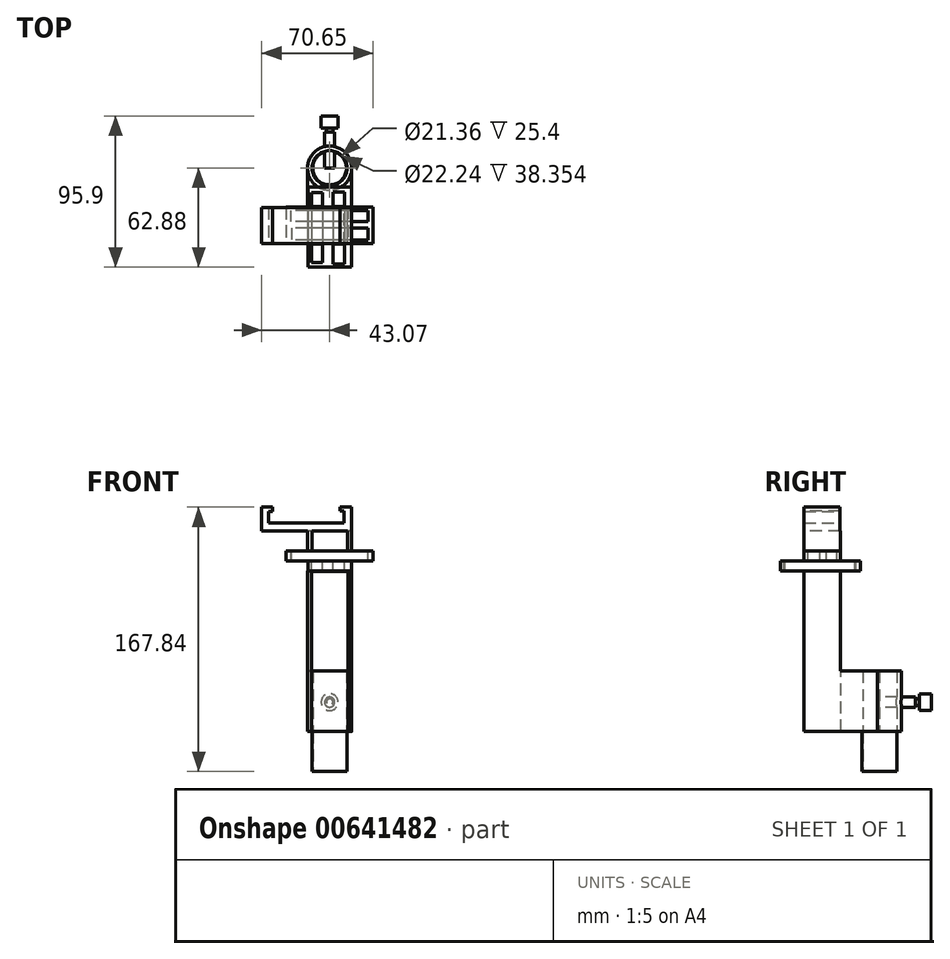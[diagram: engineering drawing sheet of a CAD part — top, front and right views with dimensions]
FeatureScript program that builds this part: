
annotation { "Feature Type Name" : "Feature", "Feature Type Description" : "" }
export const myFeature = defineFeature(function(context is Context, id is Id, definition is map)
    precondition{}
    {
        {
            var Q0;
            Q0=qCreatedBy(makeId("Top.planeOp"),FACE);
            var sketch = newSketch(context, id + "F0", { "sketchPlane" : qUnion([Q0])});
            skCircle(sketch, "E0", {"center": v(0, 0) * mm, "radius": 11.49 * mm});
            skSolve(sketch);
        }
        {
            var Q0;
            Q0=makeQuery(id+"F0.imprint","IMPRINT",FACE,{"disambiguationData":[TD([[makeQuery(id+"F0.imprint","IMPRINT",EDGE,{"derivedFrom":sQuery(id+"F0.wireOp",EDGE,"E0")}),1.0]])]});
            extrude(context, id + "F1", {"entities" : qUnion([Q0]), "depth" : 25.4 * mm, "offsetDistance" : 25.4 * mm});
        }
        {
            var Q0;
            Q0=qCreatedBy(makeId("Top.planeOp"),FACE);
            var sketch = newSketch(context, id + "F2", { "sketchPlane" : qUnion([Q0])});
            skCircle(sketch, "E1", {"center": v(0, 0) * mm, "radius": 14.04 * mm});
            skSolve(sketch);
        }
        {
            var Q0;
            Q0=makeQuery(id+"F2.imprint","IMPRINT",FACE,{"disambiguationData":[TD([[makeQuery(id+"F2.imprint","IMPRINT",EDGE,{"derivedFrom":sQuery(id+"F2.wireOp",EDGE,"E1")}),1.0]])]});
            extrude(context, id + "F3", {"entities" : qUnion([Q0]), "depth" : 38.35 * mm, "offsetDistance" : 25.4 * mm});
        }
        {
            var Q0;
            Q0=qCreatedBy(makeId("Top.planeOp"),FACE);
            var sketch = newSketch(context, id + "F4", { "sketchPlane" : qUnion([Q0])});
            skCircle(sketch, "E2", {"center": v(0, 0) * mm, "radius": 11.12 * mm});
            skSolve(sketch);
        }
        {
            var Q0;
            Q0=makeQuery(id+"F4.imprint","IMPRINT",FACE,{"disambiguationData":[TD([[makeQuery(id+"F4.imprint","IMPRINT",EDGE,{"derivedFrom":sQuery(id+"F4.wireOp",EDGE,"E2")}),1.0]])]});
            extrude(context, id + "F5", {"entities" : qUnion([Q0]), "operationType" : NewBodyOperationType.REMOVE, "depth" : 40.64 * mm, "offsetDistance" : 25.4 * mm});
        }
        {
            var Q0;
            Q0=qCreatedBy(makeId("Top.planeOp"),FACE);
            var sketch = newSketch(context, id + "F6", { "sketchPlane" : qUnion([Q0])});
            skCircle(sketch, "E3", {"center": v(0, 0) * mm, "radius": 11.14 * mm});
            skSolve(sketch);
        }
        {
            var Q0;
            Q0=makeQuery(id+"F6.imprint","IMPRINT",FACE,{"disambiguationData":[TD([[makeQuery(id+"F6.imprint","IMPRINT",EDGE,{"derivedFrom":sQuery(id+"F6.wireOp",EDGE,"E3")}),1.0]])]});
            extrude(context, id + "F7", {"entities" : qUnion([Q0]), "oppositeDirection" : true, "depth" : 25.4 * mm, "offsetDistance" : 25.4 * mm});
        }
        {
            var Q0;
            Q0=makeQuery(id+"F7.opExtrude","CAP_FACE",FACE,{"disambiguationData":[OSD([sQuery(id+"F6.wireOp",EDGE,"E3")])],"isStart":false});
            var sketch = newSketch(context, id + "F8", { "sketchPlane" : qUnion([Q0])});
            skCircle(sketch, "E4", {"center": v(0, 0) * mm, "radius": 10.68 * mm});
            skSolve(sketch);
        }
        {
            var Q0;
            Q0=makeQuery(id+"F8.imprint","IMPRINT",FACE,{"disambiguationData":[TD([[makeQuery(id+"F8.imprint","IMPRINT",EDGE,{"derivedFrom":sQuery(id+"F8.wireOp",EDGE,"E4")}),1.0]])]});
            extrude(context, id + "F9", {"entities" : qUnion([Q0]), "operationType" : NewBodyOperationType.REMOVE, "oppositeDirection" : true, "depth" : 25.4 * mm, "offsetDistance" : 25.4 * mm});
        }
        {
            var Q0;
            Q0=qCreatedBy(makeId("Right.planeOp"),FACE);
            var sketch = newSketch(context, id + "F10", { "sketchPlane" : qUnion([Q0])});
            skLineSegment(sketch, "E5.bottom", {"start": v(0, 38.3) * mm, "end": v(-48.18, 38.3) * mm});
            skLineSegment(sketch, "E5.top", {"start": v(0, 0) * mm, "end": v(-48.18, 0) * mm});
            skLineSegment(sketch, "E5.left", {"start": v(0, 38.3) * mm, "end": v(0, 0) * mm});
            skLineSegment(sketch, "E5.right", {"start": v(-48.18, 38.3) * mm, "end": v(-48.18, 0) * mm});
            skSolve(sketch);
        }
        {
            var Q0;
            Q0=makeQuery(id+"F10.imprint","IMPRINT",FACE,{"disambiguationData":[TD([[makeQuery(id+"F10.imprint","IMPRINT",EDGE,{"derivedFrom":sQuery(id+"F10.wireOp",EDGE,"E5.bottom")}),1.0]])]});
            extrude(context, id + "F11", {"entities" : qUnion([Q0]), "operationType" : NewBodyOperationType.ADD, "depth" : 13.97 * mm, "offsetDistance" : 25.4 * mm, "hasSecondDirection" : true, "secondDirectionOppositeDirection" : true, "secondDirectionDepth" : 13.97 * mm});
        }
        {
            var Q0;
            Q0=makeQuery(id+"F11.opExtrude","SWEPT_FACE",FACE,{"disambiguationData":[OSD([sQuery(id+"F10.wireOp",EDGE,"E5.bottom")])]});
            var sketch = newSketch(context, id + "F12", { "sketchPlane" : qUnion([Q0])});
            skLineSegment(sketch, "E6.bottom", {"start": v(13.97, -48.18) * mm, "end": v(-13.97, -48.18) * mm});
            skLineSegment(sketch, "E6.top", {"start": v(13.97, -24.78) * mm, "end": v(-13.97, -24.78) * mm});
            skLineSegment(sketch, "E6.left", {"start": v(13.97, -48.18) * mm, "end": v(13.97, -24.78) * mm});
            skLineSegment(sketch, "E6.right", {"start": v(-13.97, -48.18) * mm, "end": v(-13.97, -24.78) * mm});
            skSolve(sketch);
        }
        {
            var Q0;
            Q0=makeQuery(id+"F12.imprint","IMPRINT",FACE,{"disambiguationData":[TD([[makeQuery(id+"F12.imprint","IMPRINT",EDGE,{"derivedFrom":sQuery(id+"F12.wireOp",EDGE,"E6.bottom")}),-1.0]])]});
            extrude(context, id + "F13", {"entities" : qUnion([Q0]), "operationType" : NewBodyOperationType.ADD, "depth" : 63.5 * mm, "offsetDistance" : 25.4 * mm});
        }
        {
            var Q0;
            Q0=makeQuery(id+"F13.opExtrude","CAP_FACE",FACE,{"disambiguationData":[OSD([sQuery(id+"F12.wireOp",EDGE,"E6.bottom"),sQuery(id+"F12.wireOp",EDGE,"E6.top"),sQuery(id+"F12.wireOp",EDGE,"E6.left"),sQuery(id+"F12.wireOp",EDGE,"E6.right")])],"isStart":false});
            var sketch = newSketch(context, id + "F14", { "sketchPlane" : qUnion([Q0])});
            skLineSegment(sketch, "E7.bottom", {"start": v(13.78, -12.05) * mm, "end": v(-13.78, -12.05) * mm});
            skLineSegment(sketch, "E7.top", {"start": v(13.78, -62.88) * mm, "end": v(-13.78, -62.88) * mm});
            skLineSegment(sketch, "E7.left", {"start": v(13.78, -12.05) * mm, "end": v(13.78, -62.88) * mm});
            skLineSegment(sketch, "E7.right", {"start": v(-13.78, -12.05) * mm, "end": v(-13.78, -62.88) * mm});
            skPoint(sketch, "E7.middle", {"position": v(0, -37.47) * mm});
            skSolve(sketch);
        }
        {
            var Q0;
            {var subQ0=sQuery(id+"F14.wireOp",EDGE,"E7.bottom");Q0=makeQuery(id+"F14.imprint","IMPRINT",FACE,{"disambiguationData":[TD([[makeQuery(id+"F14.imprint","IMPRINT",EDGE,{"derivedFrom":subQ0}),1.0]])]});}
            var Q1;
            {var subQ0=sQuery(id+"F14.wireOp",EDGE,"E7.left");var subQ1=makeQuery(id+"F13.opExtrude","CAP_EDGE",EDGE,{"disambiguationData":[OSD([sQuery(id+"F12.wireOp",EDGE,"E6.top")])],"isStart":false});var subQ2=makeQuery(id+"F14.imprint","INTERSECT",VERTEX,{"derivedFrom":[subQ1,subQ0]});Q1=makeQuery(id+"F14.imprint","IMPRINT",FACE,{"disambiguationData":[TD([[makeQuery(id+"F14.imprint","IMPRINT",EDGE,{"disambiguationData":[TD([[subQ2,-1.0]])],"derivedFrom":subQ0}),-1.0]])]});}
            var Q2;
            {var subQ0=sQuery(id+"F14.wireOp",EDGE,"E7.top");Q2=makeQuery(id+"F14.imprint","IMPRINT",FACE,{"disambiguationData":[TD([[makeQuery(id+"F14.imprint","IMPRINT",EDGE,{"derivedFrom":subQ0}),-1.0]])]});}
            extrude(context, id + "F15", {"entities" : qUnion([Q0, Q1, Q2]), "operationType" : NewBodyOperationType.ADD, "depth" : 6.35 * mm, "offsetDistance" : 25.4 * mm});
        }
        {
            var Q0;
            Q0=makeQuery(id+"F15.opExtrude","CAP_FACE",FACE,{"disambiguationData":[OSD([sQuery(id+"F14.wireOp",EDGE,"E7.bottom"),sQuery(id+"F14.wireOp",EDGE,"E7.top"),sQuery(id+"F14.wireOp",EDGE,"E7.left"),sQuery(id+"F14.wireOp",EDGE,"E7.right")])],"isStart":false});
            var sketch = newSketch(context, id + "F16", { "sketchPlane" : qUnion([Q0])});
            skLineSegment(sketch, "E8.bottom", {"start": v(9.53, -15.14) * mm, "end": v(2.3, -15.14) * mm});
            skLineSegment(sketch, "E8.top", {"start": v(9.53, -60.82) * mm, "end": v(2.3, -60.82) * mm});
            skLineSegment(sketch, "E8.left", {"start": v(9.53, -15.14) * mm, "end": v(9.53, -60.82) * mm});
            skLineSegment(sketch, "E8.right", {"start": v(2.3, -15.14) * mm, "end": v(2.3, -60.82) * mm});
            skLineSegment(sketch, "E9.bottom", {"start": v(-4.6, -15.64) * mm, "end": v(-11.57, -15.64) * mm});
            skLineSegment(sketch, "E9.top", {"start": v(-4.6, -60.01) * mm, "end": v(-11.57, -60.01) * mm});
            skLineSegment(sketch, "E9.left", {"start": v(-4.6, -15.64) * mm, "end": v(-4.6, -60.01) * mm});
            skLineSegment(sketch, "E9.right", {"start": v(-11.57, -15.64) * mm, "end": v(-11.57, -60.01) * mm});
            skSolve(sketch);
        }
        {
            var Q0;
            Q0 = qSketchRegion(id + "F16", true);
            extrude(context, id + "F17", {"entities" : qUnion([Q0]), "operationType" : NewBodyOperationType.REMOVE, "oppositeDirection" : true, "depth" : 6.35 * mm, "offsetDistance" : 25.4 * mm});
        }
        {
            var Q0;
            Q0=makeQuery(id+"F15.opExtrude","CAP_FACE",FACE,{"disambiguationData":[OSD([sQuery(id+"F14.wireOp",EDGE,"E7.bottom"),sQuery(id+"F14.wireOp",EDGE,"E7.top"),sQuery(id+"F14.wireOp",EDGE,"E7.left"),sQuery(id+"F14.wireOp",EDGE,"E7.right")])],"isStart":false});
            var sketch = newSketch(context, id + "F18", { "sketchPlane" : qUnion([Q0])});
            skLineSegment(sketch, "E10.bottom", {"start": v(27.58, -24.72) * mm, "end": v(-27.58, -24.72) * mm});
            skLineSegment(sketch, "E10.top", {"start": v(27.58, -47.95) * mm, "end": v(-27.58, -47.95) * mm});
            skLineSegment(sketch, "E10.left", {"start": v(27.58, -24.72) * mm, "end": v(27.58, -47.95) * mm});
            skLineSegment(sketch, "E10.right", {"start": v(-27.58, -24.72) * mm, "end": v(-27.58, -47.95) * mm});
            skPoint(sketch, "E10.middle", {"position": v(0, -36.33) * mm});
            skSolve(sketch);
        }
        {
            var Q0;
            Q0 = qSketchRegion(id + "F18", true);
            extrude(context, id + "F19", {"entities" : qUnion([Q0]), "operationType" : NewBodyOperationType.ADD, "depth" : 6.35 * mm, "offsetDistance" : 25.4 * mm});
        }
        {
            var Q0;
            Q0=makeQuery(id+"F19.opExtrude","CAP_FACE",FACE,{"disambiguationData":[OSD([sQuery(id+"F18.wireOp",EDGE,"E10.bottom"),sQuery(id+"F18.wireOp",EDGE,"E10.top"),sQuery(id+"F18.wireOp",EDGE,"E10.left"),sQuery(id+"F18.wireOp",EDGE,"E10.right")])],"isStart":false});
            var sketch = newSketch(context, id + "F20", { "sketchPlane" : qUnion([Q0])});
            skLineSegment(sketch, "E11.bottom", {"start": v(24.36, -33.9) * mm, "end": v(-24.36, -33.9) * mm});
            skLineSegment(sketch, "E11.top", {"start": v(24.36, -27.03) * mm, "end": v(-24.36, -27.03) * mm});
            skLineSegment(sketch, "E11.left", {"start": v(24.36, -33.9) * mm, "end": v(24.36, -27.03) * mm});
            skLineSegment(sketch, "E11.right", {"start": v(-24.36, -33.9) * mm, "end": v(-24.36, -27.03) * mm});
            skPoint(sketch, "E11.middle", {"position": v(0, -30.46) * mm});
            skPoint(sketch, "E11.middle.positionSnap0", {"position": v(0, -24.72) * mm});
            skPoint(sketch, "E11.centerSnap0", {"position": v(0, -24.72) * mm});
            skLineSegment(sketch, "E12.bottom", {"start": v(24.3, -38.01) * mm, "end": v(-24.3, -38.01) * mm});
            skLineSegment(sketch, "E12.top", {"start": v(24.3, -45.63) * mm, "end": v(-24.3, -45.63) * mm});
            skLineSegment(sketch, "E12.left", {"start": v(24.3, -38.01) * mm, "end": v(24.3, -45.63) * mm});
            skLineSegment(sketch, "E12.right", {"start": v(-24.3, -38.01) * mm, "end": v(-24.3, -45.63) * mm});
            skPoint(sketch, "E12.middle", {"position": v(0, -41.82) * mm});
            skPoint(sketch, "E12.middle.positionSnap0", {"position": v(0, -33.9) * mm});
            skPoint(sketch, "E12.centerSnap0", {"position": v(0, -33.9) * mm});
            skSolve(sketch);
        }
        {
            var Q0;
            Q0=makeQuery(id+"F20.imprint","IMPRINT",FACE,{"disambiguationData":[TD([[makeQuery(id+"F20.imprint","IMPRINT",EDGE,{"derivedFrom":sQuery(id+"F20.wireOp",EDGE,"E11.bottom")}),-1.0]])]});
            var Q1;
            Q1=makeQuery(id+"F20.imprint","IMPRINT",FACE,{"disambiguationData":[TD([[makeQuery(id+"F20.imprint","IMPRINT",EDGE,{"derivedFrom":sQuery(id+"F20.wireOp",EDGE,"E12.bottom")}),1.0]])]});
            extrude(context, id + "F21", {"entities" : qUnion([Q0, Q1]), "operationType" : NewBodyOperationType.REMOVE, "oppositeDirection" : true, "depth" : 6.35 * mm, "offsetDistance" : 25.4 * mm});
        }
        {
            var Q0;
            Q0=makeQuery(id+"F13.boolean.opBoolean","MERGE",FACE,{"derivedFrom":[makeQuery(id+"F11.opExtrude","SWEPT_FACE",FACE,{"disambiguationData":[OSD([sQuery(id+"F10.wireOp",EDGE,"E5.right")])]}),makeQuery(id+"F13.opExtrude","SWEPT_FACE",FACE,{"disambiguationData":[OSD([sQuery(id+"F12.wireOp",EDGE,"E6.bottom")])]})]});
            var sketch = newSketch(context, id + "F22", { "sketchPlane" : qUnion([Q0])});
            skLineSegment(sketch, "E13.bottom", {"start": v(-11.56, -7.42) * mm, "end": v(11.56, -7.42) * mm});
            skLineSegment(sketch, "E13.top", {"start": v(-11.56, 101.74) * mm, "end": v(11.56, 101.74) * mm});
            skLineSegment(sketch, "E13.left", {"start": v(-11.56, -7.42) * mm, "end": v(-11.56, 101.74) * mm});
            skLineSegment(sketch, "E13.right", {"start": v(11.56, -7.42) * mm, "end": v(11.56, 101.74) * mm});
            skPoint(sketch, "E13.middle", {"position": v(0, 47.16) * mm});
            skSolve(sketch);
        }
        {
            var Q0;
            {var subQ0=sQuery(id+"F22.wireOp",EDGE,"E13.top");Q0=makeQuery(id+"F22.imprint","IMPRINT",FACE,{"disambiguationData":[TD([[makeQuery(id+"F22.imprint","IMPRINT",EDGE,{"derivedFrom":subQ0}),-1.0]])]});}
            extrude(context, id + "F23", {"entities" : qUnion([Q0]), "operationType" : NewBodyOperationType.REMOVE, "oppositeDirection" : true, "depth" : 23.62 * mm, "offsetDistance" : 25.4 * mm});
        }
        {
            var Q0;
            Q0=makeQuery(id+"F19.opExtrude","CAP_FACE",FACE,{"disambiguationData":[OSD([sQuery(id+"F18.wireOp",EDGE,"E10.bottom"),sQuery(id+"F18.wireOp",EDGE,"E10.top"),sQuery(id+"F18.wireOp",EDGE,"E10.left"),sQuery(id+"F18.wireOp",EDGE,"E10.right")])],"isStart":false});
            var sketch = newSketch(context, id + "F24", { "sketchPlane" : qUnion([Q0])});
            skLineSegment(sketch, "E14.bottom", {"start": v(-14, -24.72) * mm, "end": v(14, -24.72) * mm});
            skLineSegment(sketch, "E14.top", {"start": v(-14, -48) * mm, "end": v(14, -48) * mm});
            skLineSegment(sketch, "E14.left", {"start": v(-14, -24.72) * mm, "end": v(-14, -48) * mm});
            skLineSegment(sketch, "E14.right", {"start": v(14, -24.72) * mm, "end": v(14, -48) * mm});
            skPoint(sketch, "E14.middle", {"position": v(0, -36.36) * mm});
            skSolve(sketch);
        }
        {
            var Q0;
            Q0 = qSketchRegion(id + "F24", true);
            extrude(context, id + "F25", {"entities" : qUnion([Q0]), "operationType" : NewBodyOperationType.ADD, "depth" : 12.7 * mm, "offsetDistance" : 25.4 * mm});
        }
        {
            var Q0;
            Q0=makeQuery(id+"F25.opExtrude","CAP_FACE",FACE,{"disambiguationData":[OSD([sQuery(id+"F24.wireOp",EDGE,"E14.bottom"),sQuery(id+"F24.wireOp",EDGE,"E14.top"),sQuery(id+"F24.wireOp",EDGE,"E14.left"),sQuery(id+"F24.wireOp",EDGE,"E14.right")])],"isStart":false});
            var sketch = newSketch(context, id + "F26", { "sketchPlane" : qUnion([Q0])});
            skLineSegment(sketch, "E15.bottom", {"start": v(11.28, -50.66) * mm, "end": v(-11.28, -50.66) * mm});
            skLineSegment(sketch, "E15.top", {"start": v(11.28, -23.7) * mm, "end": v(-11.28, -23.7) * mm});
            skLineSegment(sketch, "E15.left", {"start": v(11.28, -50.66) * mm, "end": v(11.28, -23.7) * mm});
            skLineSegment(sketch, "E15.right", {"start": v(-11.28, -50.66) * mm, "end": v(-11.28, -23.7) * mm});
            skPoint(sketch, "E15.middle", {"position": v(0, -37.18) * mm});
            skSolve(sketch);
        }
        {
            var Q0;
            {var subQ0=sQuery(id+"F26.wireOp",EDGE,"E15.bottom");Q0=makeQuery(id+"F26.imprint","IMPRINT",FACE,{"disambiguationData":[TD([[makeQuery(id+"F26.imprint","IMPRINT",EDGE,{"derivedFrom":subQ0}),-1.0]])]});}
            var Q1;
            {var subQ0=sQuery(id+"F26.wireOp",EDGE,"E15.left");var subQ1=makeQuery(id+"F25.opExtrude","CAP_EDGE",EDGE,{"disambiguationData":[OSD([sQuery(id+"F24.wireOp",EDGE,"E14.top")])],"isStart":false});var subQ2=makeQuery(id+"F26.imprint","INTERSECT",VERTEX,{"derivedFrom":[subQ1,subQ0]});Q1=makeQuery(id+"F26.imprint","IMPRINT",FACE,{"disambiguationData":[TD([[makeQuery(id+"F26.imprint","IMPRINT",EDGE,{"disambiguationData":[TD([[subQ2,-1.0]])],"derivedFrom":subQ0}),1.0]])]});}
            extrude(context, id + "F27", {"entities" : qUnion([Q0, Q1]), "operationType" : NewBodyOperationType.REMOVE, "oppositeDirection" : true, "depth" : 12.7 * mm, "offsetDistance" : 25.4 * mm});
        }
        {
            var Q0;
            {var subQ0=sQuery(id+"F24.wireOp",EDGE,"E14.top");var subQ1=sQuery(id+"F24.wireOp",EDGE,"E14.right");var subQ2=sQuery(id+"F24.wireOp",EDGE,"E14.bottom");Q0=makeQuery(id+"F27.boolean.opBoolean","SPLIT",FACE,{"disambiguationData":[TD([makeQuery(id+"F25.opExtrude","SWEPT_FACE",FACE,{"disambiguationData":[OSD([subQ1])]})])],"derivedFrom":makeQuery(id+"F25.opExtrude","CAP_FACE",FACE,{"disambiguationData":[OSD([subQ2,subQ0,sQuery(id+"F24.wireOp",EDGE,"E14.left"),subQ1])],"isStart":false})});}
            var sketch = newSketch(context, id + "F28", { "sketchPlane" : qUnion([Q0])});
            skLineSegment(sketch, "E16.bottom", {"start": v(14, -48) * mm, "end": v(-43.07, -48) * mm});
            skLineSegment(sketch, "E16.top", {"start": v(14, -25.1) * mm, "end": v(-43.07, -25.1) * mm});
            skLineSegment(sketch, "E16.left", {"start": v(14, -48) * mm, "end": v(14, -25.1) * mm});
            skLineSegment(sketch, "E16.right", {"start": v(-43.07, -48) * mm, "end": v(-43.07, -25.1) * mm});
            skSolve(sketch);
        }
        {
            var Q0;
            {var subQ3=sQuery(id+"F28.wireOp",EDGE,"E16.right");Q0=makeQuery(id+"F28.imprint","IMPRINT",FACE,{"disambiguationData":[TD([[makeQuery(id+"F28.imprint","IMPRINT",EDGE,{"derivedFrom":subQ3}),-1.0]])]});}
            var Q1;
            {var subQ0=sQuery(id+"F28.wireOp",EDGE,"E16.left");Q1=makeQuery(id+"F28.imprint","IMPRINT",FACE,{"disambiguationData":[TD([[makeQuery(id+"F28.imprint","IMPRINT",EDGE,{"derivedFrom":subQ0}),-1.0]])]});}
            extrude(context, id + "F29", {"entities" : qUnion([Q0, Q1]), "operationType" : NewBodyOperationType.ADD, "depth" : 5.08 * mm, "offsetDistance" : 25.4 * mm});
        }
        {
            var Q0;
            Q0=makeQuery(id+"F29.opExtrude","CAP_FACE",FACE,{"disambiguationData":[OSD([sQuery(id+"F28.wireOp",EDGE,"E16.bottom"),sQuery(id+"F28.wireOp",EDGE,"E16.top"),sQuery(id+"F28.wireOp",EDGE,"E16.left"),sQuery(id+"F28.wireOp",EDGE,"E16.right")])],"isStart":false});
            var sketch = newSketch(context, id + "F30", { "sketchPlane" : qUnion([Q0])});
            skLineSegment(sketch, "E17.bottom", {"start": v(-43.07, -25.1) * mm, "end": v(-38.77, -25.1) * mm});
            skLineSegment(sketch, "E17.top", {"start": v(-43.07, -48) * mm, "end": v(-38.77, -48) * mm});
            skLineSegment(sketch, "E17.left", {"start": v(-43.07, -25.1) * mm, "end": v(-43.07, -48) * mm});
            skLineSegment(sketch, "E17.right", {"start": v(-38.77, -25.1) * mm, "end": v(-38.77, -48) * mm});
            skLineSegment(sketch, "E18.bottom", {"start": v(14, -48) * mm, "end": v(9.03, -48) * mm});
            skLineSegment(sketch, "E18.top", {"start": v(14, -25.1) * mm, "end": v(9.03, -25.1) * mm});
            skLineSegment(sketch, "E18.left", {"start": v(14, -48) * mm, "end": v(14, -25.1) * mm});
            skLineSegment(sketch, "E18.right", {"start": v(9.03, -48) * mm, "end": v(9.03, -25.1) * mm});
            skSolve(sketch);
        }
        {
            var Q0;
            Q0 = qSketchRegion(id + "F30", true);
            extrude(context, id + "F31", {"entities" : qUnion([Q0]), "operationType" : NewBodyOperationType.ADD, "depth" : 10.16 * mm, "offsetDistance" : 25.4 * mm});
        }
        {
            var Q0;
            Q0=makeQuery(id+"F31.opExtrude","SWEPT_FACE",FACE,{"disambiguationData":[OSD([sQuery(id+"F30.wireOp",EDGE,"E18.right")])]});
            var sketch = newSketch(context, id + "F32", { "sketchPlane" : qUnion([Q0])});
            skLineSegment(sketch, "E19.bottom", {"start": v(25.1, 142.44) * mm, "end": v(48, 142.44) * mm});
            skLineSegment(sketch, "E19.top", {"start": v(25.1, 139.88) * mm, "end": v(48, 139.88) * mm});
            skLineSegment(sketch, "E19.left", {"start": v(25.1, 142.44) * mm, "end": v(25.1, 139.88) * mm});
            skLineSegment(sketch, "E19.right", {"start": v(48, 142.44) * mm, "end": v(48, 139.88) * mm});
            skSolve(sketch);
        }
        {
            var Q0;
            Q0 = qSketchRegion(id + "F32", true);
            extrude(context, id + "F33", {"entities" : qUnion([Q0]), "operationType" : NewBodyOperationType.ADD, "depth" : 2.54 * mm, "offsetDistance" : 25.4 * mm});
        }
        {
            var Q0;
            Q0=makeQuery(id+"F31.opExtrude","SWEPT_FACE",FACE,{"disambiguationData":[OSD([sQuery(id+"F30.wireOp",EDGE,"E17.right")])]});
            var sketch = newSketch(context, id + "F34", { "sketchPlane" : qUnion([Q0])});
            skLineSegment(sketch, "E20.bottom", {"start": v(-48, 142.44) * mm, "end": v(-25.1, 142.44) * mm});
            skLineSegment(sketch, "E20.top", {"start": v(-48, 139.67) * mm, "end": v(-25.1, 139.67) * mm});
            skLineSegment(sketch, "E20.left", {"start": v(-48, 142.44) * mm, "end": v(-48, 139.67) * mm});
            skLineSegment(sketch, "E20.right", {"start": v(-25.1, 142.44) * mm, "end": v(-25.1, 139.67) * mm});
            skSolve(sketch);
        }
        {
            var Q0;
            Q0 = qSketchRegion(id + "F34", true);
            extrude(context, id + "F35", {"entities" : qUnion([Q0]), "operationType" : NewBodyOperationType.ADD, "depth" : 2.54 * mm, "offsetDistance" : 25.4 * mm});
        }
        {
            var Q0;
            Q0=qCreatedBy(makeId("Top.planeOp"),FACE);
            var sketch = newSketch(context, id + "F36", { "sketchPlane" : qUnion([Q0])});
            skCircle(sketch, "E21", {"center": v(0, 0) * mm, "radius": 10.67 * mm});
            skSolve(sketch);
        }
        {
            var Q0;
            Q0 = qSketchRegion(id + "F36", true);
            extrude(context, id + "F37", {"entities" : qUnion([Q0]), "operationType" : NewBodyOperationType.REMOVE, "depth" : 40.64 * mm, "offsetDistance" : 25.4 * mm});
        }
        {
            var Q0;
            Q0=qCreatedBy(makeId("Front.planeOp"),FACE);
            var sketch = newSketch(context, id + "F38", { "sketchPlane" : qUnion([Q0])});
            skCircle(sketch, "E22", {"center": v(0, 18.59) * mm, "radius": 3.22 * mm});
            skSolve(sketch);
        }
        {
            var Q0;
            Q0 = qSketchRegion(id + "F38", true);
            extrude(context, id + "F39", {"entities" : qUnion([Q0]), "operationType" : NewBodyOperationType.ADD, "oppositeDirection" : true, "depth" : 22.86 * mm, "offsetDistance" : 25.4 * mm});
        }
        {
            var Q0;
            Q0=makeQuery(id+"F39.opExtrude","CAP_FACE",FACE,{"disambiguationData":[OSD([sQuery(id+"F38.wireOp",EDGE,"E22")])],"isStart":false});
            var sketch = newSketch(context, id + "F40", { "sketchPlane" : qUnion([Q0])});
            skCircle(sketch, "E23", {"center": v(0, 18.59) * mm, "radius": 2.08 * mm});
            skSolve(sketch);
        }
        {
            var Q0;
            Q0 = qSketchRegion(id + "F40", true);
            extrude(context, id + "F41", {"entities" : qUnion([Q0]), "operationType" : NewBodyOperationType.ADD, "depth" : 2.54 * mm, "offsetDistance" : 25.4 * mm});
        }
        {
            var Q0;
            Q0=makeQuery(id+"F41.opExtrude","CAP_FACE",FACE,{"disambiguationData":[OSD([sQuery(id+"F40.wireOp",EDGE,"E23")])],"isStart":false});
            var sketch = newSketch(context, id + "F42", { "sketchPlane" : qUnion([Q0])});
            skCircle(sketch, "E24", {"center": v(0, 18.59) * mm, "radius": 5.39 * mm});
            skSolve(sketch);
        }
        {
            var Q0;
            Q0 = qSketchRegion(id + "F42", true);
            extrude(context, id + "F43", {"entities" : qUnion([Q0]), "operationType" : NewBodyOperationType.ADD, "depth" : 7.62 * mm, "offsetDistance" : 25.4 * mm});
        }
    });
